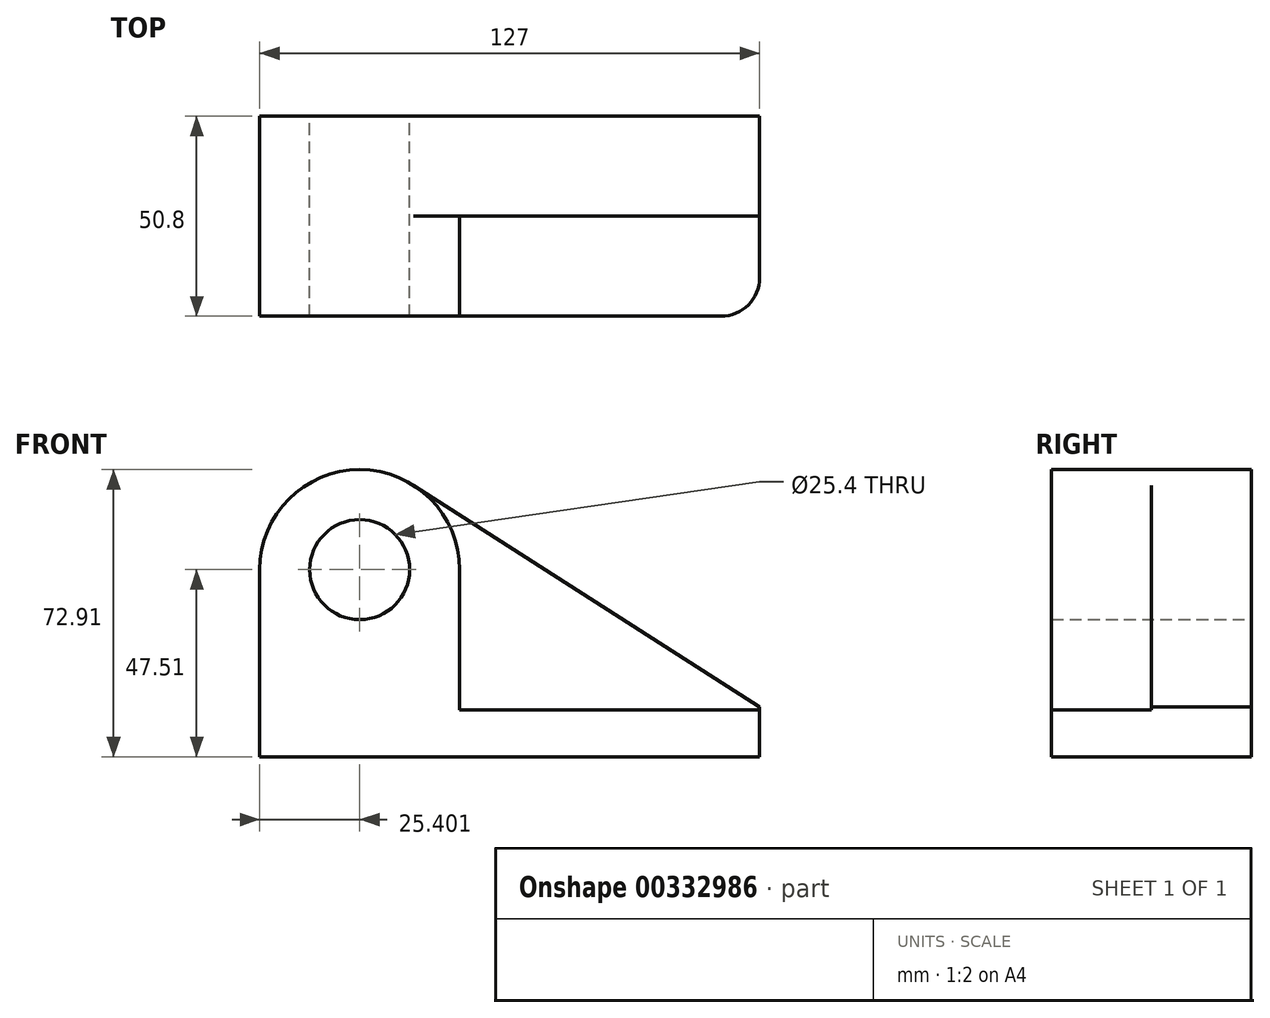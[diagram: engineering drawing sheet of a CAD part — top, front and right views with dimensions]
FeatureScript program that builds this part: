
annotation { "Feature Type Name" : "Feature", "Feature Type Description" : "" }
export const myFeature = defineFeature(function(context is Context, id is Id, definition is map)
    precondition{}
    {
        {
            var Q0;
            Q0=qCreatedBy(makeId("Front.planeOp"),FACE);
            var sketch = newSketch(context, id + "F0", { "sketchPlane" : qUnion([Q0])});
            skCircle(sketch, "E0", {"center": v(-51.53, 50.8) * mm, "radius": 12.7 * mm});
            skArc(sketch, "E1", {"start": v(-37.85, 72.2) * mm, "mid": v(-63.73, 73.08) * mm, "end": v(-76.93, 50.8) * mm});
            skLineSegment(sketch, "E2", {"start": v(-51.53, 50.8) * mm, "end": v(-76.93, 50.8) * mm});
            skLineSegment(sketch, "E3", {"start": v(-76.93, 50.8) * mm, "end": v(-76.93, 0) * mm});
            skLineSegment(sketch, "E4", {"start": v(-76.93, 0) * mm, "end": v(0, 0) * mm});
            skLineSegment(sketch, "E5", {"start": v(-76.93, 3.29) * mm, "end": v(50.07, 3.29) * mm});
            skLineSegment(sketch, "E6", {"start": v(50.07, 3.29) * mm, "end": v(50.07, 15.99) * mm});
            skLineSegment(sketch, "E7", {"start": v(50.07, 15.99) * mm, "end": v(-38.8, 72.81) * mm});
            skSolve(sketch);
        }
        {
            var Q0;
            Q0=makeQuery(id+"F0.imprint","IMPRINT",FACE,{"disambiguationData":[TD([[makeQuery(id+"F0.imprint","IMPRINT",EDGE,{"derivedFrom":sQuery(id+"F0.wireOp",EDGE,"E0")}),-1.0]])]});
            extrude(context, id + "F1", {"entities" : qUnion([Q0]), "depth" : 25.4 * mm});
        }
        {
            var Q0;
            Q0=makeQuery(id+"F1.opExtrude","CAP_FACE",FACE,{"disambiguationData":[OSD([sQuery(id+"F0.wireOp",EDGE,"E0"),sQuery(id+"F0.wireOp",EDGE,"E1"),sQuery(id+"F0.wireOp",EDGE,"E3"),sQuery(id+"F0.wireOp",EDGE,"E5"),sQuery(id+"F0.wireOp",EDGE,"E6"),sQuery(id+"F0.wireOp",EDGE,"E7")])],"isStart":false});
            var sketch = newSketch(context, id + "F2", { "sketchPlane" : qUnion([Q0])});
            skCircle(sketch, "E8", {"center": v(-51.53, 50.8) * mm, "radius": 12.7 * mm});
            skArc(sketch, "E9", {"start": v(-26.13, 50.8) * mm, "mid": v(-51.53, 76.2) * mm, "end": v(-76.93, 50.8) * mm});
            skLineSegment(sketch, "E10.bottom", {"start": v(50.07, 3.29) * mm, "end": v(-76.93, 3.29) * mm});
            skLineSegment(sketch, "E10.top", {"start": v(50.07, 15.17) * mm, "end": v(-26.13, 15.17) * mm});
            skLineSegment(sketch, "E10.left", {"start": v(50.07, 3.29) * mm, "end": v(50.07, 15.17) * mm});
            skLineSegment(sketch, "E10.right", {"start": v(-76.93, 3.29) * mm, "end": v(-76.93, 15.17) * mm});
            skLineSegment(sketch, "E11", {"start": v(-76.93, 50.8) * mm, "end": v(-76.93, 15.17) * mm});
            skLineSegment(sketch, "E12", {"start": v(-26.13, 50.8) * mm, "end": v(-26.13, 15.99) * mm});
            skLineSegment(sketch, "E13", {"start": v(-26.13, 15.99) * mm, "end": v(-26.13, 15.17) * mm});
            skPoint(sketch, "E13.endSnap0", {"position": v(-26.13, 33.4) * mm});
            skPoint(sketch, "E14.orphan", {"position": v(-26.13, 8.5) * mm});
            skSolve(sketch);
        }
        {
            var Q0;
            Q0=makeQuery(id+"F2.imprint","IMPRINT",FACE,{"disambiguationData":[TD([[makeQuery(id+"F2.imprint","IMPRINT",EDGE,{"derivedFrom":sQuery(id+"F2.wireOp",EDGE,"E8")}),-1.0]])]});
            extrude(context, id + "F3", {"entities" : qUnion([Q0]), "operationType" : NewBodyOperationType.ADD, "depth" : 25.4 * mm});
        }
        {
            var Q0;
            Q0=makeQuery(id+"F3.opExtrude","CAP_EDGE",EDGE,{"disambiguationData":[OSD([sQuery(id+"F2.wireOp",EDGE,"E10.left")])],"isStart":false});
            fillet(context, id + "F4", {"entities" : qUnion([Q0]), "radius" : 9.8 * mm, "tangentPropagation" : true, "allowEdgeOverflow" : false});
        }
    });
